# Revit family: Grab_Bar-Bariatric-Bradley_Corp-8320
name_source: partatom
category: Specialty Equipment
revit_build: Autodesk Revit 2017 (Build: 20160225_1515(x64)
units: mm (PartAtom-declared; Revit-internal decimal feet)

## family parameters
Cut with Voids When Loaded = No
Host = Face
OmniClass Number = 23.40.20.21.47
OmniClass Title = Bath Grab Bars
Part Type = Normal
Room Calculation Point = No
Round Connector Dimension = Use Diameter
Shared = No

## types (2) — shared parameters
ADA Compliant = Yes
Assembly Code = C1030200
Bar Material = Metal - Bradley Corp - Stainless Steel - Satin
Default Elevation = 33 "
Depth = 2.75 "
Height = 3.125 "
LEED Credit = 0
Low Emitting Material = No
Manufacturer = Bradley Corporation
Manufacturer Installation URL - English = https://www.bradleycorp.com
MasterFormat Number = 10 28 00
MasterFormat Title = Toilet, Bath, and Laundry Accessories
OmniClass Table 21 Number = 21-03 10 90 40
OmniClass Table 21 Title = Toilet, Bath, and Laundry Accessories
OmniClass Table 23 Number = 23.40.20.21.47
OmniClass Table 23 Title = Bath Grab Bars
Product Page URL = https://www.bradleycorp.com
Product Tech Data URL - English = https://www.bradleycorp.com
Specifications URL = http://www.bradleycorp.com
URL = http://www.bradleycorp.com
Version = 1.0
Warranty Information = Complete Unit 1 Year Warranty. This Warranty does not cover installation or any other labor charges and does not apply to any units which have been damaged by abuse, improper installation, imporper maintanence, or altered in any way.
zero-valued in all types: Percentage of Recycled Content

## per-type parameters (varying)
| type | Description | Width | z Center Support Visible | z Number of Flanges | z Wall Support Spacing |
| 8320-106420 | 1-1/4" x 42" Long Bariatric Grab Bar with 3 Supports | 42 " | Yes | 5 | 10.5 " |
| 8320-106360 | 1-1/4" x 36" Long Bariatric Grab Bar with 3 Supports | 36 " | No | 4 | 12 " |

note: column(s) folded — value = type name in every type: Model

## geometry (parser evidence)
native form markers: Blend x8, Sweep x1
no freeform markers — native parametric forms only
